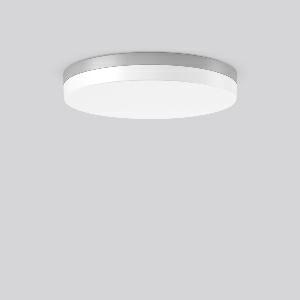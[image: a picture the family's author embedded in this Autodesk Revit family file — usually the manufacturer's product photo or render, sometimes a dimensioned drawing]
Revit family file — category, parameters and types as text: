
# Revit family: flat_slim_round_312634_004_1_19_8b8f
name_source: partatom
category: Lighting Fixtures
units: mm (PartAtom-declared; Revit-internal decimal feet)

## family parameters
Cut with Voids When Loaded = No
Host = Face
Light Source = No
Part Type = Normal
Room Calculation Point = No
Round Connector Dimension = Use Diameter
Shared = No

## types (1)
- MultiLumen 1 830 (1 x LED Modul 830, 3500 lm, 3000)
    Apparent Load = 24 VA
    CIE Flux Codes = 38 68 89 85 100
    Color Rendering = 80
    Color Temperature = 3000
    Default Elevation = 1800 mm
    Height = 70 mm
    Lamp = 1 x LED Modul 830
    Lamp Light Flux = 3500 lm
    Lamp count = 1
    Length = 480 mm
    Lifetime = 50000 h
    Luminous efficacy = 146 lm/W
    Manufacturer = RZB
    ModVariant = No
    Model = 312634.004.1.19
    Mounting Place = Ceiling
    Mounting Type = Surface mounted
    Number of Poles = 1
    OnlyDefault = Yes
    Power Factor = 1
    Product Name = FLAT SLIM round
    Product group = Surface mounted ceiling and wall luminaires
    ProductGroupID = 305
    Protection Class = Protection class I
    Protection Degree = Degree of protection
    RLX_Detail_Level = 1
    RLX_Emergency_Light_Flux = 0 lm
    RLX_Emergency_Type = 0
    RLX_Emergency_Type_DB = No
    RlxData = <blob elided: 22677 chars, md5=c53d7b6b>
    Socket = socket
    Standby Power = 0 W
    System Light Flux = 3500 lm
    System Power = 24 W
    Type Comments = MultiLumen 1 830
    Type Image = 312633.004.jpg
    URL = http://relux.com
    VarID = multilumen_1_830
    Voltage = 0 V
    Weight = 0.00 kg
    Width = 0 mm  [stored 0 ft]

note: [stored X ft] marks values corroborated as IEEE doubles in the binary element streams (Revit-internal decimal feet)

## geometry (parser evidence)
native form markers: Blend x4, Sweep x13
no freeform markers — native parametric forms only
